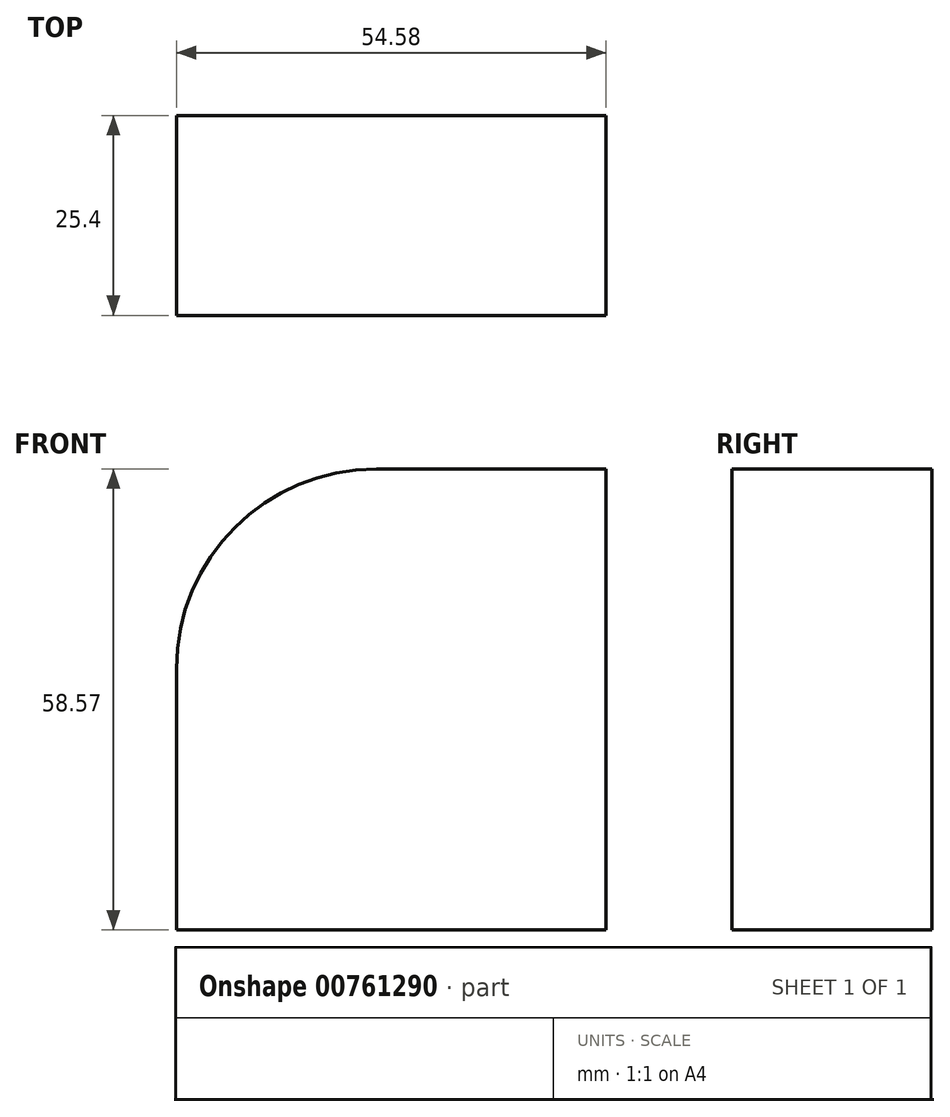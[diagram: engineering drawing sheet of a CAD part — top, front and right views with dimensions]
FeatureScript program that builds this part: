
annotation { "Feature Type Name" : "Feature", "Feature Type Description" : "" }
export const myFeature = defineFeature(function(context is Context, id is Id, definition is map)
    precondition{}
    {
        {
            var Q0;
            Q0=qCreatedBy(makeId("Front.planeOp"),FACE);
            var sketch = newSketch(context, id + "F0", { "sketchPlane" : qUnion([Q0])});
            skLineSegment(sketch, "E0.bottom", {"start": v(0, 0) * mm, "end": v(54.58, 0) * mm});
            skLineSegment(sketch, "E0.top", {"start": v(25.4, 58.57) * mm, "end": v(54.58, 58.57) * mm});
            skLineSegment(sketch, "E0.left", {"start": v(0, 0) * mm, "end": v(0, 33.17) * mm});
            skLineSegment(sketch, "E0.right", {"start": v(54.58, 0) * mm, "end": v(54.58, 58.57) * mm});
            skPoint(sketch, "E1.visualSharp", {"position": v(0, 58.57) * mm});
            skArc(sketch, "E1.filletArc", {"start": v(25.4, 58.57) * mm, "mid": v(7.44, 51.13) * mm, "end": v(0, 33.17) * mm});
            skSolve(sketch);
        }
        {
            var Q0;
            Q0=makeQuery(id+"F0.imprint","IMPRINT",FACE,{"disambiguationData":[TD([[makeQuery(id+"F0.imprint","IMPRINT",EDGE,{"derivedFrom":sQuery(id+"F0.wireOp",EDGE,"E0.bottom")}),1.0]])]});
            extrude(context, id + "F1", {"entities" : qUnion([Q0]), "depth" : 25.4 * mm, "offsetDistance" : 25.4 * mm});
        }
    });
